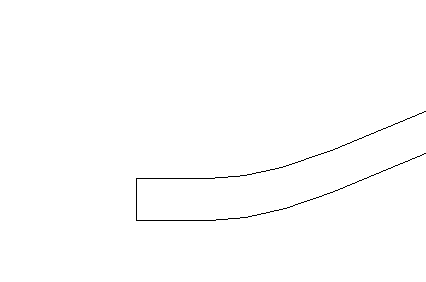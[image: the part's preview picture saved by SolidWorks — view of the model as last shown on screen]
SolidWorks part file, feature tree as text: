
SOLIDWORKS PART (.sldprt)
format: sldprt  version: not decoded by parser v0  size: 70,144 bytes
history: native  units: mm
features: sketch x165, extrude x1 + 2 further entries (+11 scaffold rows collapsed; 10 parser-record rows omitted)
feature tree (189):
  scaffold x11  (default folders/planes/origin — collapsed)
  sketch  "Sketch1"  dims[c1.D1=~24.323482mm c2.D1=3.0mm c2.D2=10.0mm c2.D3=5.0mm c2.D4=3.0mm c2.D5=40.0mm c2.D6=10.0mm c2.D7=5.0mm c2.D8=10.0mm]
  extrude  "Extrude1"  Depth=10mm cosMaterialEX=210000000000.0
  sketch  "cosMaterialNUXY"
  sketch  "cosMaterialGXY"
  sketch  "cosMaterialALPX"
  sketch  "cosMaterialDENS"
  sketch  "cosMaterialKX"
  sketch  "cosMaterialC"
  sketch  "Units"
  sketch  "AnalysisType"
  sketch  "MeshType"
  sketch  "cosMaterialSIGYLD"
  sketch  "cosMaterialSIGXT"
  sketch  "cosMaterialSIGXC"  dims[sMaterialName=0.0mm cosFMVItemName=0.0mm cosMaterialName=0.0mm cosComponentName=0.0mm]
  sketch  "cosMaterialEX"
  sketch  "cosMaterialNUXY"
  sketch  "cosMaterialGXY"
  sketch  "cosMaterialALPX"
  sketch  "cosMaterialDENS"
  sketch  "cosMaterialKX"
  sketch  "cosMaterialC"
  sketch  "Units"
  sketch  "AnalysisType"
  sketch  "MeshType"
  sketch  "cosMaterialSIGYLD"
  sketch  "cosMaterialSIGXT"
  sketch  "cosMaterialSIGXC"  dims[sMaterialSourceName=0.0mm sMaterialName=0.0mm cosFMVItemName=0.0mm cosMaterialName=0.0mm cosComponentName=0.0mm]
  "pé3mm:Restraint-1"
  sketch  "RestraintType"
  sketch  "Value"
  sketch  "cosRestraintComp:1"
  sketch  "cosRestraintComp:2"
  sketch  "cosRestraintComp:3"
  sketch  "cosRestraintComp:4"
  sketch  "cosRestraintComp:5"
  sketch  "cosRestraintComp:6"
  sketch  "Unit"
  sketch  "AnalysisType"
  sketch  "MeshType"
  sketch  "cosRestraintCompCheck1"
  sketch  "cosRestraintCompCheck2"
  sketch  "cosRestraintCompCheck3"
  sketch  "cosRestraintCompCheck4"
  sketch  "cosRestraintCompCheck5"
  sketch  "cosRestraintCompCheck6"
  sketch  "cosRestraintRefPlaneSet"
  sketch  "cosRestraintRefPlaneOrigin1"
  sketch  "cosRestraintRefPlaneOrigin2"
  sketch  "cosRestraintRefPlaneOrigin3"
  sketch  "cosRestraintRefPlaneXDir1"
  sketch  "cosRestraintRefPlaneXDir2"
  sketch  "cosRestraintRefPlaneXDir3"
  sketch  "cosRestraintRefPlaneNormal1"
  sketch  "cosRestraintRefPlaneNormal2"
  sketch  "cosRestraintRefPlaneNormal3"  dims[cosRestraintRefPlaneName=0.0mm]
  sketch  "cosRestraintCoordSystemType"
  sketch  "cosRestraintFaceTypeMask"  dims[cosFMVItemName=0.0mm cosRestraint4=0.0]
  sketch  "RestraintType"
  sketch  "Value"
  sketch  "cosRestraintComp:1"
  sketch  "cosRestraintComp:2"
  sketch  "cosRestraintComp:3"
  sketch  "cosRestraintComp:4"
  sketch  "cosRestraintComp:5"
  sketch  "cosRestraintComp:6"
  sketch  "Unit"
  sketch  "AnalysisType"
  sketch  "MeshType"
  sketch  "cosRestraintCompCheck1"
  sketch  "cosRestraintCompCheck2"
  sketch  "cosRestraintCompCheck3"
  sketch  "cosRestraintCompCheck4"
  sketch  "cosRestraintCompCheck5"
  sketch  "cosRestraintCompCheck6"
  sketch  "cosRestraintRefPlaneSet"
  sketch  "cosRestraintRefPlaneOrigin1"
  sketch  "cosRestraintRefPlaneOrigin2"
  sketch  "cosRestraintRefPlaneOrigin3"
  sketch  "cosRestraintRefPlaneXDir1"
  sketch  "cosRestraintRefPlaneXDir2"
  sketch  "cosRestraintRefPlaneXDir3"
  sketch  "cosRestraintRefPlaneNormal1"
  sketch  "cosRestraintRefPlaneNormal2"
  sketch  "cosRestraintRefPlaneNormal3"  dims[cosRestraintRefPlaneName=0.0mm]
  sketch  "cosRestraintCoordSystemType"
  sketch  "cosRestraintFaceTypeMask"  dims[cosFMVItemName=0.0mm]
  "pé3mm:Force-1"
  sketch  "cosForceComp:1"
  sketch  "cosForceComp:2"
  sketch  "cosForceComp:3"
  sketch  "cosForceComp:4"
  sketch  "cosForceComp:5"
  sketch  "cosForceComp:6"
  sketch  "cosForceTorqueNF"
  sketch  "cosForceCompCheck1"
  sketch  "cosForceCompCheck2"
  sketch  "cosForceCompCheck3"
  sketch  "cosForceCompCheck4"
  sketch  "cosForceCompCheck5"
  sketch  "cosForceCompCheck6"
  sketch  "Unit"
  sketch  "AnalysisType"
  sketch  "MeshType"
  sketch  "cosForceRefPlaneSet"
  sketch  "cosForceRefPlaneOrigin1"
  sketch  "cosForceRefPlaneOrigin2"
  sketch  "cosForceRefPlaneOrigin3"
  sketch  "cosForceRefPlaneXDir1"
  sketch  "cosForceRefPlaneXDir2"
  sketch  "cosForceRefPlaneXDir3"
  sketch  "cosForceRefPlaneNormal1"
  sketch  "cosForceRefPlaneNormal2"
  sketch  "cosForceRefPlaneNormal3"  dims[cosForceRefPlaneName=0.0mm]
  sketch  "cosForceCoordSystemType"
  sketch  "cosForceType"  dims[cosFMVItemName=0.0mm]
  sketch  "cosDistributionType"  dims[cosDistributionCoordSysName=0.0mm]
  sketch  "cosDistributionCoef1"
  sketch  "cosDistributionCoef2"
  sketch  "cosDistributionCoef3"
  sketch  "cosDistributionCoef4"
  sketch  "cosDistributionCoef5"
  sketch  "cosDistributionCoef6"  dims[cosForce5=0.0]
  sketch  "cosForceComp:1"
  sketch  "cosForceComp:2"
  sketch  "cosForceComp:3"
  sketch  "cosForceComp:4"
  sketch  "cosForceComp:5"
  sketch  "cosForceComp:6"
  sketch  "cosForceTorqueNF"
  sketch  "cosForceCompCheck1"
  sketch  "cosForceCompCheck2"
  sketch  "cosForceCompCheck3"
  sketch  "cosForceCompCheck4"
  sketch  "cosForceCompCheck5"
  sketch  "cosForceCompCheck6"
  sketch  "Unit"
  sketch  "AnalysisType"
  sketch  "MeshType"
  sketch  "cosForceRefPlaneSet"
  sketch  "cosForceRefPlaneOrigin1"
  sketch  "cosForceRefPlaneOrigin2"
  sketch  "cosForceRefPlaneOrigin3"
  sketch  "cosForceRefPlaneXDir1"
  sketch  "cosForceRefPlaneXDir2"
  sketch  "cosForceRefPlaneXDir3"
  sketch  "cosForceRefPlaneNormal1"
  sketch  "cosForceRefPlaneNormal2"
  sketch  "cosForceRefPlaneNormal3"  dims[cosForceRefPlaneName=0.0mm]
  sketch  "cosForceCoordSystemType"
  sketch  "cosForceType"  dims[cosFMVItemName=0.0mm]
  sketch  "cosDistributionType"  dims[cosDistributionCoordSysName=0.0mm]
  sketch  "cosDistributionCoef1"
  sketch  "cosDistributionCoef2"
  sketch  "cosDistributionCoef3"
  sketch  "cosDistributionCoef4"
  sketch  "cosDistributionCoef5"
  sketch  "cosDistributionCoef6"
  parser-record x10  (decoder bookkeeping rows leaked as tree rows — omitted from the tree; the rows remain in map.json)
  sketch  "faceID"  dims[cosFaceID=0.0]
  sketch  "faceID"
  sketch  "faceID"
  sketch  "faceID"
  sketch  "faceID"
  sketch  "faceID"
  sketch  "faceID"
  sketch  "faceID"
  sketch  "faceID"
  sketch  "faceID"
  sketch  "faceID"
decode coverage: 16 of 166 modeling features carry decoded parameters; 2 rows unclassified (native names shown)
note: ~ marks probable driven/reference dimensions
note: suppression state not decoded; provenance and decode notes live in map.json
